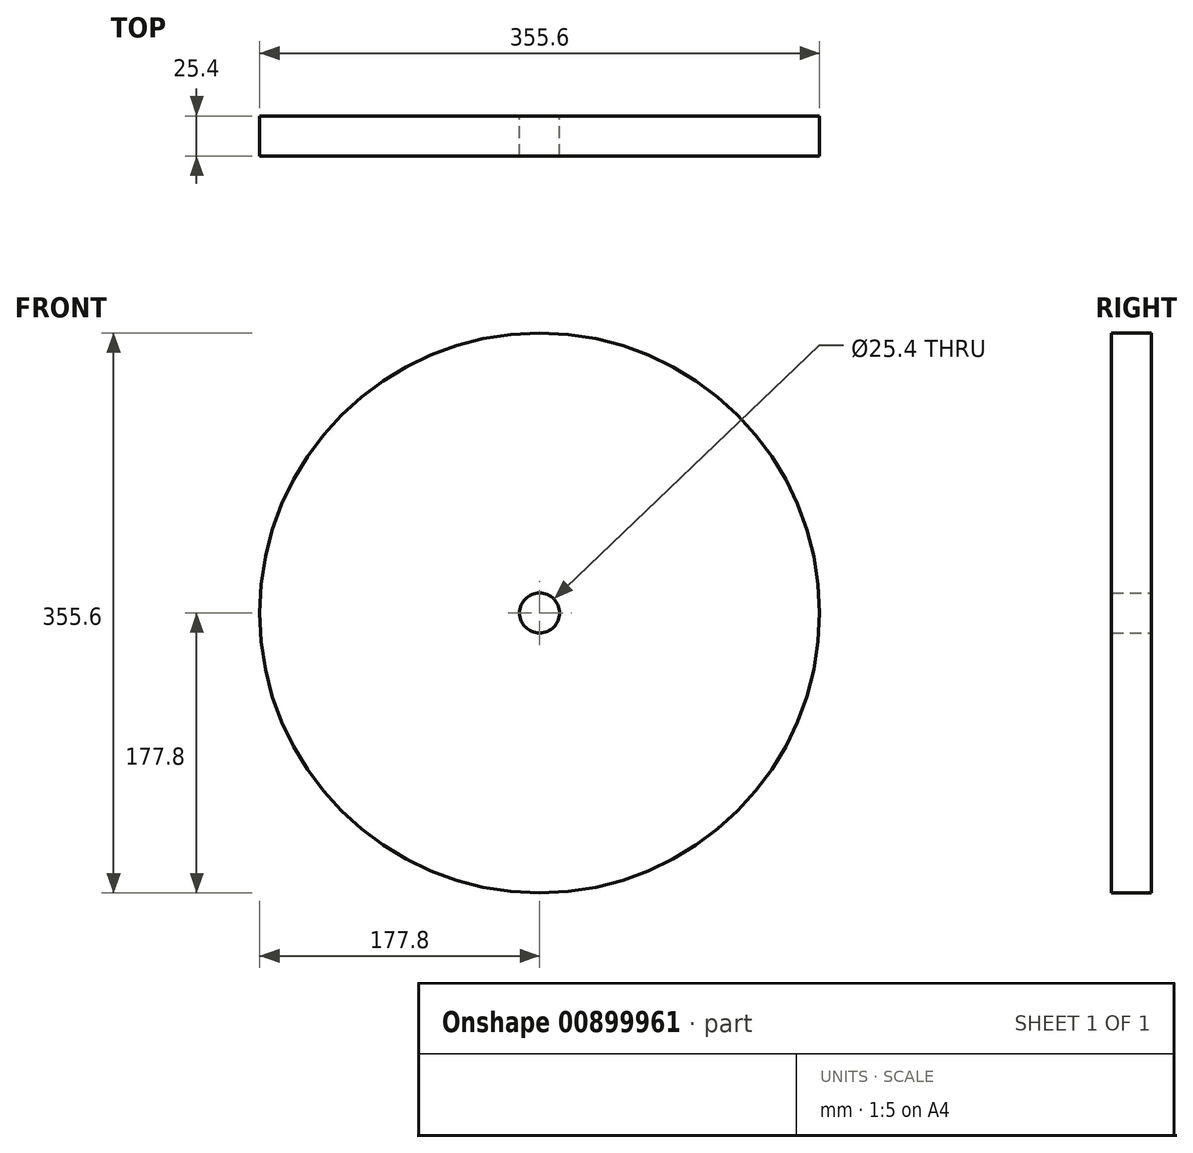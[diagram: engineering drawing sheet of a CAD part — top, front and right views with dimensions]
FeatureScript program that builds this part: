
annotation { "Feature Type Name" : "Feature", "Feature Type Description" : "" }
export const myFeature = defineFeature(function(context is Context, id is Id, definition is map)
    precondition{}
    {
        {
            var Q0;
            Q0=qCreatedBy(makeId("Front.planeOp"),FACE);
            var sketch = newSketch(context, id + "F0", { "sketchPlane" : qUnion([Q0])});
            skCircle(sketch, "E0", {"center": v(0, 0) * mm, "radius": 177.8 * mm});
            skCircle(sketch, "E1", {"center": v(0, 0) * mm, "radius": 12.7 * mm});
            skSolve(sketch);
        }
        {
            var Q0;
            Q0 = qSketchRegion(id + "F0", true);
            extrude(context, id + "F1", {"entities" : qUnion([Q0]), "depth" : 25.4 * mm, "offsetDistance" : 25.4 * mm});
        }
    });
